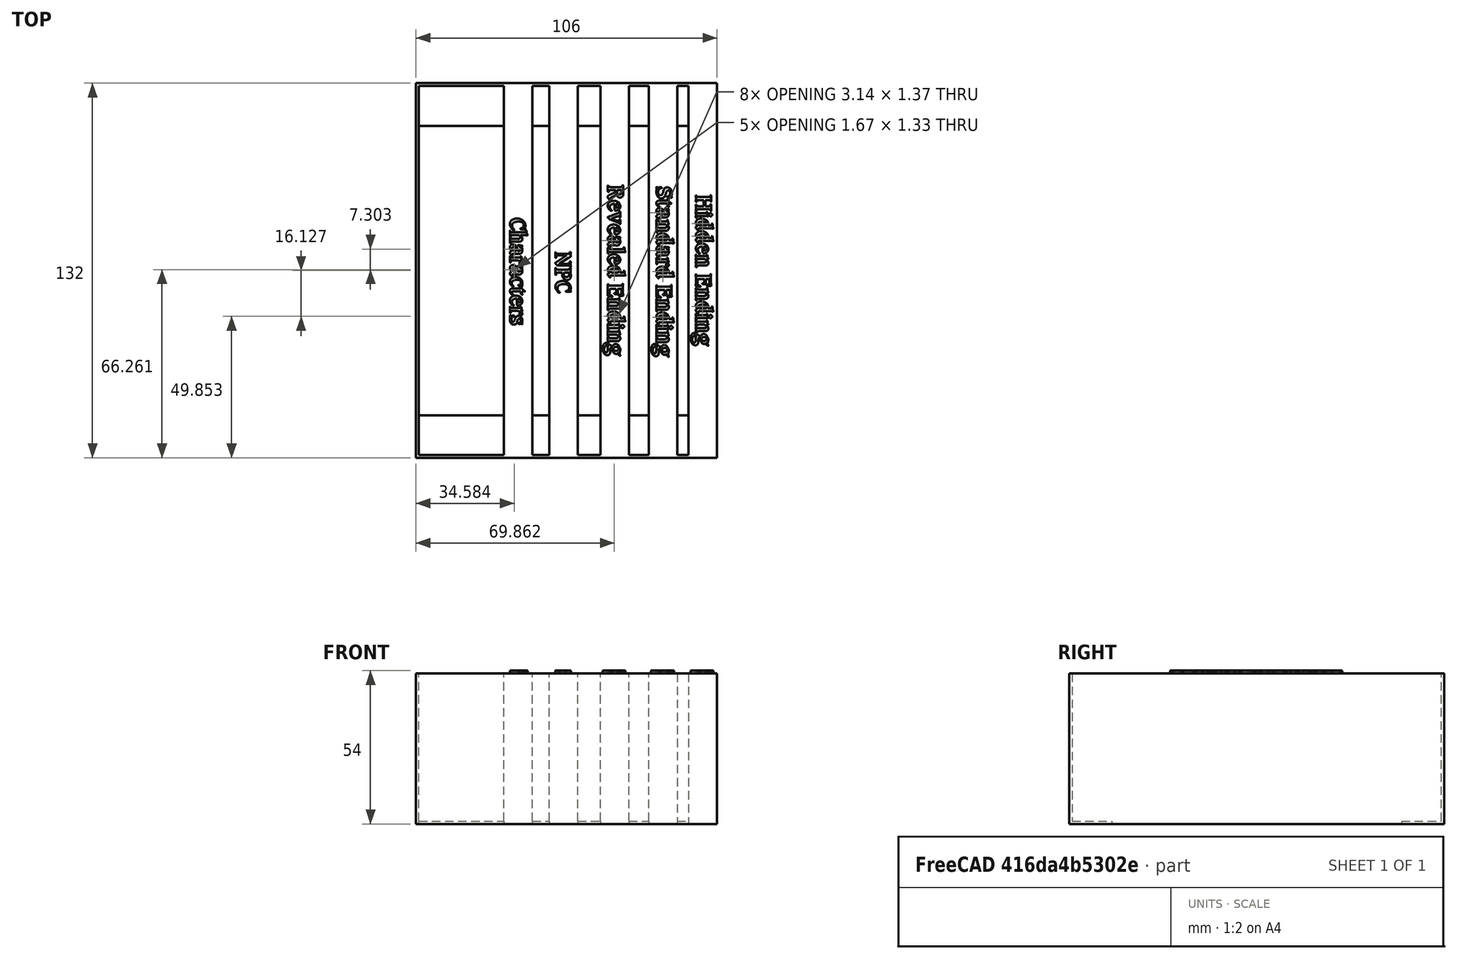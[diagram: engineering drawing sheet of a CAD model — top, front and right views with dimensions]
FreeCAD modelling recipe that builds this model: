
FCSTD DOCUMENT  (FreeCAD 0.18R4 (GitTag))
Label: characters
License: All rights reserved
LicenseURL: http://en.wikipedia.org/wiki/All_rights_reserved
objects: Part::Box×10, Part::Part2DObjectPython×5, Part::Extrusion×5, Part::MultiFuse×3, Part::Cut×2
note: 25 computed .brp shape members not serialized (recipe doc carries the construction recipe); baked Part::Feature solids carry a one-line shape summary decoded from their .brp

FEATURE [Part::Box] Box  label="Cube"
  AttacherType = Attacher::AttachEngine3D
  Height = 53
  Length = 307
  Placement = pos=(1,1,0) rot=(0,0,1;0rad)
  Width = 130
FEATURE [Part::Box] Box001  label="Cube001"
  AttacherType = Attacher::AttachEngine3D
  Height = 53
  Length = 309
  Width = 132
FEATURE [Part::Cut] Cut
  Base = -> Box001
  Tool = -> Box
FEATURE [Part::Box] Box002  label="Cube002"
  AttacherType = Attacher::AttachEngine3D
  Height = 1
  Length = 309
  Width = 15
FEATURE [Part::Box] Box003  label="Cube003"
  AttacherType = Attacher::AttachEngine3D
  Height = 1
  Length = 309
  Placement = pos=(0,117,0) rot=(0,0,1;0rad)
  Width = 15
FEATURE [Part::MultiFuse] Fusion
  Shapes = -> [Cut,Box002,Box003]
FEATURE [Part::Box] Box004  label="Cube004"
  AttacherType = Attacher::AttachEngine3D
  Height = 53
  Length = 10
  Placement = pos=(31,0,0) rot=(0,0,1;0rad)
  Width = 131
FEATURE [Part::Box] Box005  label="Cube005"
  AttacherType = Attacher::AttachEngine3D
  Height = 53
  Length = 10
  Placement = pos=(47,0,0) rot=(0,0,1;0rad)
  Width = 131
FEATURE [Part::Box] Box006  label="Cube006"
  AttacherType = Attacher::AttachEngine3D
  Height = 53
  Length = 10
  Placement = pos=(65,0,0) rot=(0,0,1;0rad)
  Width = 131
FEATURE [Part::Box] Box007  label="Cube007"
  AttacherType = Attacher::AttachEngine3D
  Height = 53
  Length = 10
  Placement = pos=(82,0,0) rot=(0,0,1;0rad)
  Width = 131
FEATURE [Part::Box] Box008  label="Cube008"
  AttacherType = Attacher::AttachEngine3D
  Height = 53
  Length = 10
  Placement = pos=(96,0,0) rot=(0,0,1;0rad)
  Width = 131
FEATURE [Part::Box] Box009  label="Cube009"
  AttacherType = Attacher::AttachEngine3D
  Height = 53
  Length = 212
  Placement = pos=(106,0,0) rot=(0,0,1;0rad)
  Width = 132
FEATURE [Part::MultiFuse] Fusion001
  Shapes = -> [Fusion,Box008,Box005,Box007,Box006,Box004]
FEATURE [Part::Part2DObjectPython] ShapeString  # Draft 2D object (typed FeaturePython)
  FontFile = <userpath>/Downloads/talisman/Caxton Bold.otf
  Placement = pos=(36.2,99.64,53) rot=(0,0,-1;1.5708rad)
  Size = 3
  String = Characters
  Tracking = 0
FEATURE [Part::Part2DObjectPython] ShapeString001  # Draft 2D object (typed FeaturePython)
  FontFile = <userpath>/Downloads/talisman/Caxton Bold.otf
  Placement = pos=(49.2,99.64,53) rot=(0,0,-1;1.5708rad)
  Size = 3
  String = NPC
  Tracking = 0
FEATURE [Part::Part2DObjectPython] ShapeString002  # Draft 2D object (typed FeaturePython)
  FontFile = <userpath>/Downloads/talisman/Caxton Bold.otf
  Placement = pos=(68.2,99.64,53) rot=(0,0,-1;1.5708rad)
  Size = 3
  String = Revealed Ending
  Tracking = 0
FEATURE [Part::Part2DObjectPython] ShapeString003  # Draft 2D object (typed FeaturePython)
  FontFile = <userpath>/Downloads/talisman/Caxton Bold.otf
  Placement = pos=(99.2,99.64,53) rot=(0,0,-1;1.5708rad)
  Size = 3
  String = Hidden Ending
  Tracking = 0
FEATURE [Part::Part2DObjectPython] ShapeString004  # Draft 2D object (typed FeaturePython)
  FontFile = <userpath>/Downloads/talisman/Caxton Bold.otf
  Placement = pos=(85.2,99.64,53) rot=(0,0,-1;1.5708rad)
  Size = 3
  String = Standard Ending
  Tracking = 0
FEATURE [Part::Extrusion] Extrude
  Base = -> ShapeString
  Dir = (0,0,1)
  DirMode = 2
  FaceMakerClass = Part::FaceMakerBullseye
  LengthFwd = 1
  LengthRev = 0
  Placement = pos=(-3,-15,0) rot=(0,0,1;0rad)
  Solid = false
  Symmetric = false
FEATURE [Part::Extrusion] Extrude001
  Base = -> ShapeString001
  Dir = (0,0,1)
  DirMode = 2
  FaceMakerClass = Part::FaceMakerBullseye
  LengthFwd = 1
  LengthRev = 0
  Placement = pos=(0,-27,0) rot=(0,0,1;0rad)
  Solid = false
  Symmetric = false
FEATURE [Part::Extrusion] Extrude002
  Base = -> ShapeString002
  Dir = (0,0,1)
  DirMode = 2
  FaceMakerClass = Part::FaceMakerBullseye
  LengthFwd = 1
  LengthRev = 0
  Placement = pos=(-0.5,-3.5,0) rot=(0,0,1;0rad)
  Solid = false
  Symmetric = false
FEATURE [Part::Extrusion] Extrude003
  Base = -> ShapeString003
  Dir = (0,0,1)
  DirMode = 2
  FaceMakerClass = Part::FaceMakerBullseye
  LengthFwd = 1
  LengthRev = 0
  Placement = pos=(-0.5,-7,0) rot=(0,0,1;0rad)
  Solid = false
  Symmetric = false
FEATURE [Part::Extrusion] Extrude004
  Base = -> ShapeString004
  Dir = (0,0,1)
  DirMode = 2
  FaceMakerClass = Part::FaceMakerBullseye
  LengthFwd = 1
  LengthRev = 0
  Placement = pos=(-0.4,-4,0) rot=(0,0,1;0rad)
  Solid = false
  Symmetric = false
FEATURE [Part::MultiFuse] Fusion003
  Shapes = -> [Extrude,Extrude001,Extrude003,Extrude004,Extrude002]
FEATURE [Part::Cut] Cut001
  Base = -> Fusion001
  Tool = -> Box009
